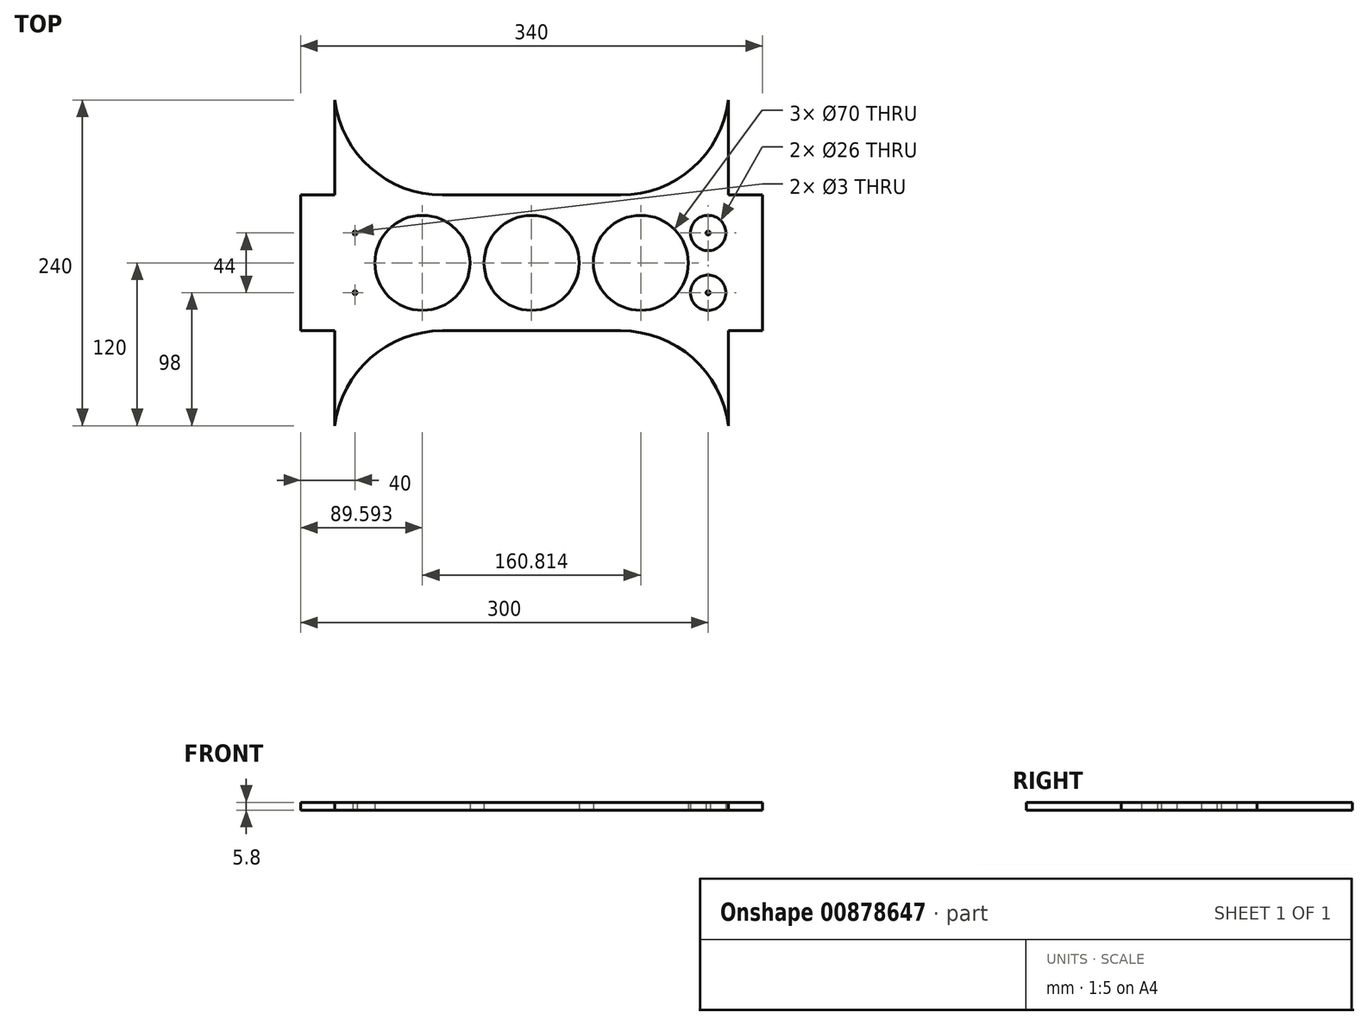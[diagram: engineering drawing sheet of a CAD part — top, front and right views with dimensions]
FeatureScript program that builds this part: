
annotation { "Feature Type Name" : "Feature", "Feature Type Description" : "" }
export const myFeature = defineFeature(function(context is Context, id is Id, definition is map)
    precondition{}
    {
        {
            var Q0;
            Q0=qCreatedBy(makeId("Top.planeOp"),FACE);
            var sketch = newSketch(context, id + "F0", { "sketchPlane" : qUnion([Q0])});
            skLineSegment(sketch, "E0.bottom", {"start": v(170, -50) * mm, "end": v(-170, -50) * mm});
            skLineSegment(sketch, "E0.top", {"start": v(170, 50) * mm, "end": v(-170, 50) * mm});
            skLineSegment(sketch, "E0.left", {"start": v(170, -50) * mm, "end": v(170, 50) * mm});
            skLineSegment(sketch, "E0.right", {"start": v(-170, -50) * mm, "end": v(-170, 50) * mm});
            skPoint(sketch, "E0.middle", {"position": v(0, 0) * mm});
            skLineSegment(sketch, "E1.bottom", {"start": v(-170, 50) * mm, "end": v(-145, 50) * mm});
            skLineSegment(sketch, "E1.top", {"start": v(-170, 120) * mm, "end": v(-145, 120) * mm});
            skLineSegment(sketch, "E1.left", {"start": v(-170, 50) * mm, "end": v(-170, 120) * mm});
            skLineSegment(sketch, "E1.right", {"start": v(-145, 50) * mm, "end": v(-145, 120) * mm});
            skLineSegment(sketch, "E2.bottom", {"start": v(170, 50) * mm, "end": v(145, 50) * mm});
            skLineSegment(sketch, "E2.top", {"start": v(170, 120) * mm, "end": v(145, 120) * mm});
            skLineSegment(sketch, "E2.left", {"start": v(170, 50) * mm, "end": v(170, 120) * mm});
            skLineSegment(sketch, "E2.right", {"start": v(145, 50) * mm, "end": v(145, 120) * mm});
            skLineSegment(sketch, "E3.bottom", {"start": v(170, -50) * mm, "end": v(145, -50) * mm});
            skLineSegment(sketch, "E3.top", {"start": v(170, -120) * mm, "end": v(145, -120) * mm});
            skLineSegment(sketch, "E3.left", {"start": v(170, -50) * mm, "end": v(170, -120) * mm});
            skLineSegment(sketch, "E3.right", {"start": v(145, -50) * mm, "end": v(145, -120) * mm});
            skLineSegment(sketch, "E4.bottom", {"start": v(-170, -50) * mm, "end": v(-145, -50) * mm});
            skLineSegment(sketch, "E4.top", {"start": v(-170, -120) * mm, "end": v(-145, -120) * mm});
            skLineSegment(sketch, "E4.left", {"start": v(-170, -50) * mm, "end": v(-170, -120) * mm});
            skLineSegment(sketch, "E4.right", {"start": v(-145, -50) * mm, "end": v(-145, -120) * mm});
            skLineSegment(sketch, "E5.bottom", {"start": v(-145, 50) * mm, "end": v(-65.63, 50) * mm});
            skLineSegment(sketch, "E5.left", {"start": v(-145, 50) * mm, "end": v(-145, 78.14) * mm});
            skLineSegment(sketch, "E6.left", {"start": v(145, 50) * mm, "end": v(145, 75.77) * mm});
            skLineSegment(sketch, "E7.bottom", {"start": v(117.5, -35) * mm, "end": v(-117.5, -35) * mm});
            skLineSegment(sketch, "E7.top", {"start": v(117.5, 35) * mm, "end": v(-117.5, 35) * mm});
            skLineSegment(sketch, "E7.left", {"start": v(117.5, -35) * mm, "end": v(117.5, 35) * mm});
            skLineSegment(sketch, "E7.right", {"start": v(-117.5, -35) * mm, "end": v(-117.5, 35) * mm});
            skCircle(sketch, "E8", {"center": v(0, 0) * mm, "radius": 35 * mm});
            skCircle(sketch, "E9", {"center": v(80.4, 0) * mm, "radius": 35 * mm});
            skLineSegment(sketch, "E10", {"start": v(0, 0) * mm, "end": v(80.4, 0) * mm});
            skLineSegment(sketch, "E11", {"start": v(0, 0) * mm, "end": v(-80.4, 0) * mm});
            skCircle(sketch, "E12", {"center": v(-80.4, 0) * mm, "radius": 35 * mm});
            skLineSegment(sketch, "E13", {"start": v(170, 0) * mm, "end": v(135, 0) * mm});
            skLineSegment(sketch, "E14", {"start": v(-170, 0) * mm, "end": v(-135, 0) * mm});
            skLineSegment(sketch, "E15", {"start": v(-135, 0) * mm, "end": v(-135, -16) * mm});
            skLineSegment(sketch, "E16", {"start": v(-135, 0) * mm, "end": v(-135, 16) * mm});
            skPoint(sketch, "E17.start.orphan", {"position": v(157.5, -120) * mm});
            skLineSegment(sketch, "E18", {"start": v(157.5, -120) * mm, "end": v(157.5, -112.5) * mm});
            skLineSegment(sketch, "E19", {"start": v(157.5, -112.5) * mm, "end": v(163.5, -112.5) * mm});
            skLineSegment(sketch, "E20", {"start": v(157.5, -112.5) * mm, "end": v(151.5, -112.5) * mm});
            skCircle(sketch, "E21", {"center": v(163.5, -112.5) * mm, "radius": 3.5 * mm});
            skCircle(sketch, "E22", {"center": v(151.5, -112.5) * mm, "radius": 3.5 * mm});
            skCircle(sketch, "E23.MirrorC", {"center": v(163.5, 112.5) * mm, "radius": 3.5 * mm});
            skCircle(sketch, "E24.MirrorC", {"center": v(151.5, 112.5) * mm, "radius": 3.5 * mm});
            skCircle(sketch, "E25.MirrorC", {"center": v(-151.5, -112.5) * mm, "radius": 3.5 * mm});
            skCircle(sketch, "E26.MirrorC", {"center": v(-163.5, -112.5) * mm, "radius": 3.5 * mm});
            skCircle(sketch, "E27.MirrorC", {"center": v(-163.5, 112.5) * mm, "radius": 3.5 * mm});
            skCircle(sketch, "E28.MirrorC", {"center": v(-151.5, 112.5) * mm, "radius": 3.5 * mm});
            skLineSegment(sketch, "E29", {"start": v(-128.35, -45.23) * mm, "end": v(-117.5, -45.23) * mm});
            skLineSegment(sketch, "E30", {"start": v(-117.5, -45.23) * mm, "end": v(-117.5, -47.73) * mm});
            skLineSegment(sketch, "E31", {"start": v(-128.35, -35.23) * mm, "end": v(-130.85, -35.23) * mm});
            skLineSegment(sketch, "E32", {"start": v(-130.85, -35.23) * mm, "end": v(-130.85, -47.73) * mm});
            skLineSegment(sketch, "E33", {"start": v(-130.85, -47.73) * mm, "end": v(-117.5, -47.73) * mm});
            skLineSegment(sketch, "E34.MirrorCS", {"start": v(130.85, -47.73) * mm, "end": v(117.5, -47.73) * mm});
            skLineSegment(sketch, "E35.MirrorCS", {"start": v(128.35, -45.23) * mm, "end": v(117.5, -45.23) * mm});
            skLineSegment(sketch, "E36.MirrorCS", {"start": v(130.85, -35.23) * mm, "end": v(130.85, -47.73) * mm});
            skLineSegment(sketch, "E37.MirrorCS", {"start": v(117.5, -45.23) * mm, "end": v(117.5, -47.73) * mm});
            skLineSegment(sketch, "E38.MirrorCS", {"start": v(128.35, -35.23) * mm, "end": v(130.85, -35.23) * mm});
            skLineSegment(sketch, "E39.MirrorCS", {"start": v(-130.85, 35.23) * mm, "end": v(-130.85, 47.73) * mm});
            skLineSegment(sketch, "E40.MirrorCS", {"start": v(-128.35, 35.23) * mm, "end": v(-130.85, 35.23) * mm});
            skLineSegment(sketch, "E41.MirrorCS", {"start": v(-117.5, 45.23) * mm, "end": v(-117.5, 47.73) * mm});
            skLineSegment(sketch, "E42.MirrorCS", {"start": v(130.85, 47.73) * mm, "end": v(117.5, 47.73) * mm});
            skLineSegment(sketch, "E43.MirrorCS", {"start": v(128.35, 45.23) * mm, "end": v(117.5, 45.23) * mm});
            skLineSegment(sketch, "E44.MirrorCS", {"start": v(130.85, 35.23) * mm, "end": v(130.85, 47.73) * mm});
            skLineSegment(sketch, "E45.MirrorCS", {"start": v(128.35, 35.23) * mm, "end": v(130.85, 35.23) * mm});
            skLineSegment(sketch, "E46.MirrorCS", {"start": v(117.5, 45.23) * mm, "end": v(117.5, 47.73) * mm});
            skPoint(sketch, "E47.MirrorCS.end.orphan", {"position": v(-117.5, 45.23) * mm});
            skPoint(sketch, "E47.MirrorCS.start.orphan", {"position": v(-128.35, 45.23) * mm});
            skPoint(sketch, "E48.MirrorCS.end.orphan", {"position": v(-117.5, 47.73) * mm});
            skPoint(sketch, "E48.MirrorCS.start.orphan", {"position": v(-130.85, 47.73) * mm});
            skPoint(sketch, "E49.MirrorCS.start.orphan", {"position": v(-128.35, 35.23) * mm});
            skPoint(sketch, "E50.MirrorCS.end.orphan", {"position": v(128.35, -45.23) * mm});
            skPoint(sketch, "E50.MirrorCS.start.orphan", {"position": v(128.35, -35.23) * mm});
            skPoint(sketch, "E51.MirrorCS.end.orphan", {"position": v(128.35, 45.23) * mm});
            skPoint(sketch, "E51.MirrorCS.start.orphan", {"position": v(128.35, 35.23) * mm});
            skArc(sketch, "E52", {"start": v(-145, 120) * mm, "mid": v(-118.54, 70) * mm, "end": v(-65.63, 50) * mm});
            skArc(sketch, "E53.MirrorCS", {"start": v(145, 120) * mm, "mid": v(118.54, 70) * mm, "end": v(65.63, 50) * mm});
            skArc(sketch, "E54.MirrorCS", {"start": v(145, -120) * mm, "mid": v(118.54, -70) * mm, "end": v(65.63, -50) * mm});
            skArc(sketch, "E55.MirrorCS", {"start": v(-145, -120) * mm, "mid": v(-118.54, -70) * mm, "end": v(-65.63, -50) * mm});
            skSolve(sketch);
        }
        {
            var Q0;
            Q0=makeQuery(id+"F0.imprint","IMPRINT",FACE,{"disambiguationData":[TD([[makeQuery(id+"F0.imprint","IMPRINT",EDGE,{"derivedFrom":sQuery(id+"F0.wireOp",EDGE,"E1.right")}),-1.0]])]});
            var Q1;
            Q1=makeQuery(id+"F0.imprint","IMPRINT",FACE,{"disambiguationData":[TD([[makeQuery(id+"F0.imprint","IMPRINT",EDGE,{"derivedFrom":sQuery(id+"F0.wireOp",EDGE,"E1.bottom")}),1.0]])]});
            var Q2;
            Q2=makeQuery(id+"F0.imprint","IMPRINT",FACE,{"disambiguationData":[TD([[makeQuery(id+"F0.imprint","IMPRINT",EDGE,{"derivedFrom":sQuery(id+"F0.wireOp",EDGE,"E0.top")}),1.0]])]});
            var Q3;
            Q3=makeQuery(id+"F0.imprint","IMPRINT",FACE,{"disambiguationData":[TD([[makeQuery(id+"F0.imprint","IMPRINT",EDGE,{"derivedFrom":sQuery(id+"F0.wireOp",EDGE,"E4.bottom")}),-1.0]])]});
            var Q4;
            {var subQ0=sQuery(id+"F0.wireOp",EDGE,"E4.right");Q4=makeQuery(id+"F0.imprint","IMPRINT",FACE,{"disambiguationData":[TD([[makeQuery(id+"F0.imprint","IMPRINT",EDGE,{"derivedFrom":subQ0}),1.0]])]});}
            var Q5;
            {var subQ0=sQuery(id+"F0.wireOp",EDGE,"E3.right");Q5=makeQuery(id+"F0.imprint","IMPRINT",FACE,{"disambiguationData":[TD([[makeQuery(id+"F0.imprint","IMPRINT",EDGE,{"derivedFrom":subQ0}),-1.0]])]});}
            var Q6;
            Q6=makeQuery(id+"F0.imprint","IMPRINT",FACE,{"disambiguationData":[TD([[makeQuery(id+"F0.imprint","IMPRINT",EDGE,{"derivedFrom":sQuery(id+"F0.wireOp",EDGE,"E3.bottom")}),1.0]])]});
            var Q7;
            Q7=makeQuery(id+"F0.imprint","IMPRINT",FACE,{"disambiguationData":[TD([[makeQuery(id+"F0.imprint","IMPRINT",EDGE,{"derivedFrom":sQuery(id+"F0.wireOp",EDGE,"E2.right")}),1.0]])]});
            var Q8;
            Q8=makeQuery(id+"F0.imprint","IMPRINT",FACE,{"disambiguationData":[TD([[makeQuery(id+"F0.imprint","IMPRINT",EDGE,{"derivedFrom":sQuery(id+"F0.wireOp",EDGE,"E2.bottom")}),-1.0]])]});
            var Q9;
            {var subQ0=sQuery(id+"F0.wireOp",EDGE,"E7.right");Q9=makeQuery(id+"F0.imprint","IMPRINT",FACE,{"disambiguationData":[TD([[makeQuery(id+"F0.imprint","IMPRINT",EDGE,{"derivedFrom":subQ0}),-1.0]])]});}
            var Q10;
            {var subQ0=sQuery(id+"F0.wireOp",EDGE,"E8");var subQ1=sQuery(id+"F0.wireOp",EDGE,"E7.top");var subQ2=makeQuery(id+"F0.imprint","INTERSECT",VERTEX,{"derivedFrom":[subQ1,subQ0]});Q10=makeQuery(id+"F0.imprint","IMPRINT",FACE,{"disambiguationData":[TD([[makeQuery(id+"F0.imprint","IMPRINT",EDGE,{"disambiguationData":[TD([[subQ2,-1.0]])],"derivedFrom":subQ1}),1.0]])]});}
            var Q11;
            {var subQ0=sQuery(id+"F0.wireOp",EDGE,"E8");var subQ1=sQuery(id+"F0.wireOp",EDGE,"E7.bottom");var subQ2=makeQuery(id+"F0.imprint","INTERSECT",VERTEX,{"derivedFrom":[subQ1,subQ0]});Q11=makeQuery(id+"F0.imprint","IMPRINT",FACE,{"disambiguationData":[TD([[makeQuery(id+"F0.imprint","IMPRINT",EDGE,{"disambiguationData":[TD([[subQ2,-1.0]])],"derivedFrom":subQ1}),-1.0]])]});}
            var Q12;
            {var subQ0=sQuery(id+"F0.wireOp",EDGE,"E9");var subQ1=sQuery(id+"F0.wireOp",EDGE,"E7.bottom");var subQ2=makeQuery(id+"F0.imprint","INTERSECT",VERTEX,{"derivedFrom":[subQ1,subQ0]});Q12=makeQuery(id+"F0.imprint","IMPRINT",FACE,{"disambiguationData":[TD([[makeQuery(id+"F0.imprint","IMPRINT",EDGE,{"disambiguationData":[TD([[subQ2,-1.0]])],"derivedFrom":subQ1}),-1.0]])]});}
            var Q13;
            {var subQ0=sQuery(id+"F0.wireOp",EDGE,"E9");var subQ1=sQuery(id+"F0.wireOp",EDGE,"E7.top");var subQ2=makeQuery(id+"F0.imprint","INTERSECT",VERTEX,{"derivedFrom":[subQ1,subQ0]});Q13=makeQuery(id+"F0.imprint","IMPRINT",FACE,{"disambiguationData":[TD([[makeQuery(id+"F0.imprint","IMPRINT",EDGE,{"disambiguationData":[TD([[subQ2,-1.0]])],"derivedFrom":subQ1}),1.0]])]});}
            var Q14;
            {var subQ0=sQuery(id+"F0.wireOp",EDGE,"E7.left");Q14=makeQuery(id+"F0.imprint","IMPRINT",FACE,{"disambiguationData":[TD([[makeQuery(id+"F0.imprint","IMPRINT",EDGE,{"derivedFrom":subQ0}),1.0]])]});}
            extrude(context, id + "F1", {"entities" : qUnion([Q0, Q1, Q2, Q3, Q4, Q5, Q6, Q7, Q8, Q9, Q10, Q11, Q12, Q13, Q14]), "depth" : 5.8 * mm, "offsetDistance" : 25 * mm});
        }
        {
            var Q0;
            Q0=makeQuery(id+"F1.opExtrude","CAP_FACE",FACE,{"disambiguationData":[OSD([sQuery(id+"F0.wireOp",EDGE,"E0.bottom"),sQuery(id+"F0.wireOp",EDGE,"E0.top"),sQuery(id+"F0.wireOp",EDGE,"E0.left"),sQuery(id+"F0.wireOp",EDGE,"E0.right"),sQuery(id+"F0.wireOp",EDGE,"E1.top"),sQuery(id+"F0.wireOp",EDGE,"E1.left"),sQuery(id+"F0.wireOp",EDGE,"E2.top"),sQuery(id+"F0.wireOp",EDGE,"E2.left"),sQuery(id+"F0.wireOp",EDGE,"E3.top"),sQuery(id+"F0.wireOp",EDGE,"E3.left"),sQuery(id+"F0.wireOp",EDGE,"E4.top"),sQuery(id+"F0.wireOp",EDGE,"E4.left"),sQuery(id+"F0.wireOp",EDGE,"b6foxv17-MAYw-Bogs-ApA3-eAK8yi2ZaEWz"),sQuery(id+"F0.wireOp",EDGE,"jrnCVo5r-84Hl-XDZ9-gl8t-09PTq8q3obiW"),sQuery(id+"F0.wireOp",EDGE,"4b0af7c1-43d4-4e40-a447-87acfc0b781e0.MirrorCS"),sQuery(id+"F0.wireOp",EDGE,"b8fc22d4-89a2-49ab-be03-c5205da13d580.MirrorCS"),sQuery(id+"F0.wireOp",EDGE,"E8"),sQuery(id+"F0.wireOp",EDGE,"E9"),sQuery(id+"F0.wireOp",EDGE,"E12"),sQuery(id+"F0.wireOp",EDGE,"E23.MirrorC"),sQuery(id+"F0.wireOp",EDGE,"E24.MirrorC"),sQuery(id+"F0.wireOp",EDGE,"E25.MirrorC"),sQuery(id+"F0.wireOp",EDGE,"E26.MirrorC"),sQuery(id+"F0.wireOp",EDGE,"E21"),sQuery(id+"F0.wireOp",EDGE,"E22"),sQuery(id+"F0.wireOp",EDGE,"E27.MirrorC"),sQuery(id+"F0.wireOp",EDGE,"E28.MirrorC")])],"isStart":true});
            var sketch = newSketch(context, id + "F2", { "sketchPlane" : qUnion([Q0])});
            skLineSegment(sketch, "E56", {"start": v(-170, 0) * mm, "end": v(-130, 0) * mm});
            skLineSegment(sketch, "E57", {"start": v(-130, 0) * mm, "end": v(-130, 22) * mm});
            skLineSegment(sketch, "E58", {"start": v(-130, 0) * mm, "end": v(-130, -22) * mm});
            skCircle(sketch, "E59", {"center": v(-130, 22) * mm, "radius": 13 * mm});
            skCircle(sketch, "E60", {"center": v(-130, -22) * mm, "radius": 13 * mm});
            skCircle(sketch, "E61", {"center": v(-130, -22) * mm, "radius": 1.5 * mm});
            skCircle(sketch, "E62", {"center": v(-130, 22) * mm, "radius": 1.5 * mm});
            skCircle(sketch, "E63.MirrorC", {"center": v(130, 22) * mm, "radius": 13 * mm});
            skCircle(sketch, "E64.MirrorC", {"center": v(130, -22) * mm, "radius": 13 * mm});
            skCircle(sketch, "E65.MirrorC", {"center": v(130, 22) * mm, "radius": 1.5 * mm});
            skCircle(sketch, "E66.MirrorC", {"center": v(130, -22) * mm, "radius": 1.5 * mm});
            skSolve(sketch);
        }
        {
            var Q0;
            Q0=makeQuery(id+"F2.imprint","IMPRINT",FACE,{"disambiguationData":[TD([[makeQuery(id+"F2.imprint","IMPRINT",EDGE,{"derivedFrom":sQuery(id+"F2.wireOp",EDGE,"E65.MirrorC")}),-1.0]])]});
            var Q1;
            Q1=makeQuery(id+"F2.imprint","IMPRINT",FACE,{"disambiguationData":[TD([[makeQuery(id+"F2.imprint","IMPRINT",EDGE,{"derivedFrom":sQuery(id+"F2.wireOp",EDGE,"E66.MirrorC")}),-1.0]])]});
            var Q2;
            Q2=makeQuery(id+"F2.imprint","IMPRINT",FACE,{"disambiguationData":[TD([[makeQuery(id+"F2.imprint","IMPRINT",EDGE,{"derivedFrom":sQuery(id+"F2.wireOp",EDGE,"E61")}),1.0]])]});
            var Q3;
            Q3=makeQuery(id+"F2.imprint","IMPRINT",FACE,{"disambiguationData":[TD([[makeQuery(id+"F2.imprint","IMPRINT",EDGE,{"derivedFrom":sQuery(id+"F2.wireOp",EDGE,"E62")}),1.0]])]});
            extrude(context, id + "F3", {"entities" : qUnion([Q0, Q1, Q2, Q3]), "operationType" : NewBodyOperationType.REMOVE, "oppositeDirection" : true, "depth" : 25 * mm, "offsetDistance" : 25 * mm});
        }
    });
